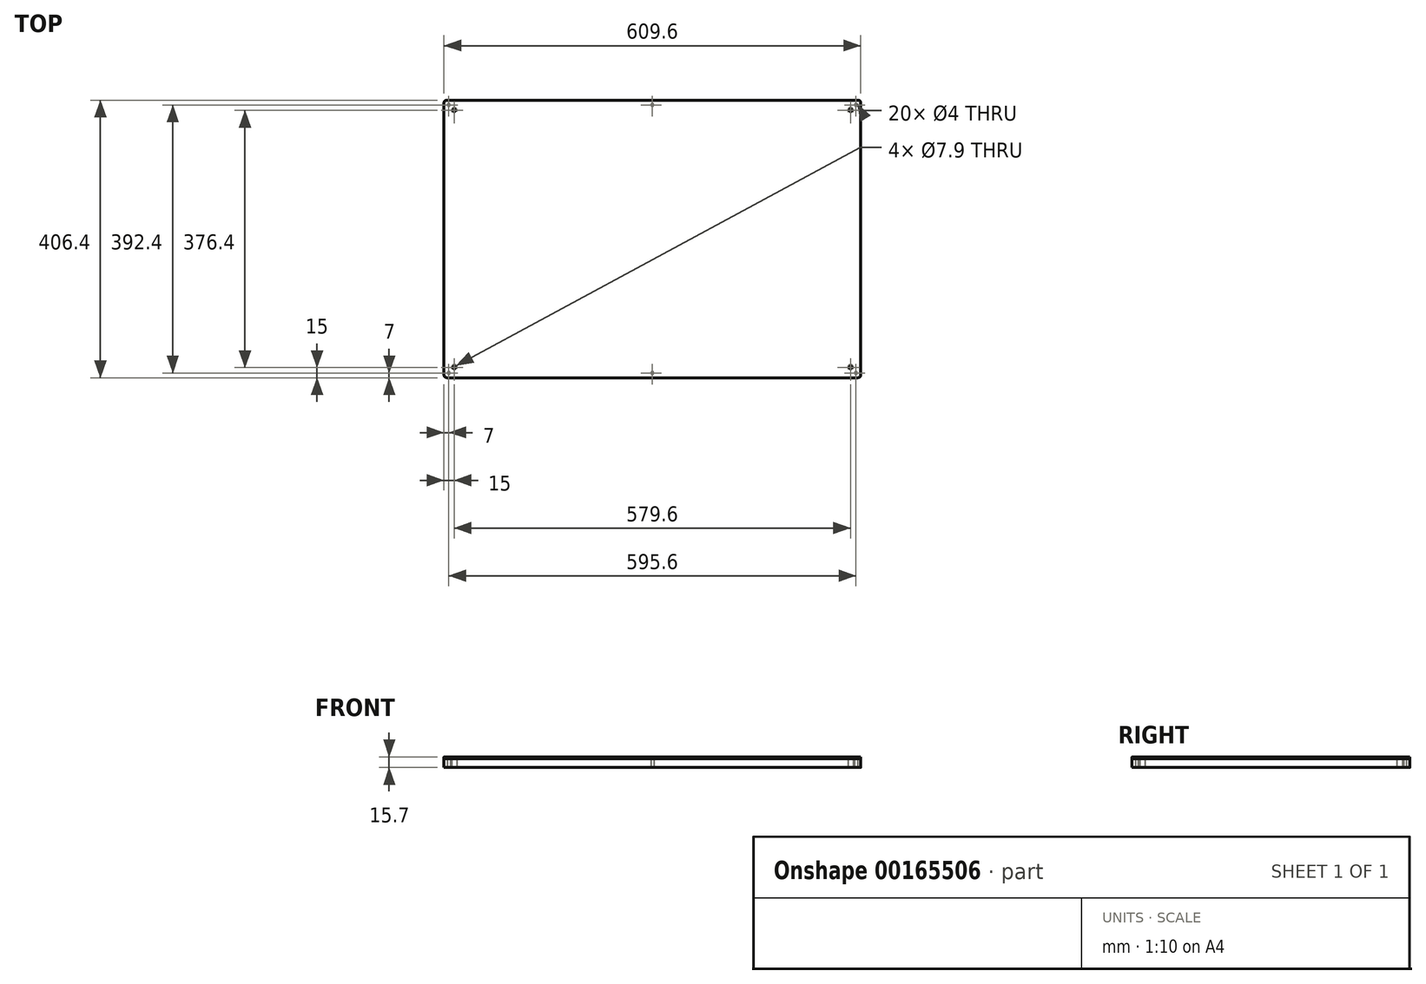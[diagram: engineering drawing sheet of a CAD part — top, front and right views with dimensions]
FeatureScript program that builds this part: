
annotation { "Feature Type Name" : "Feature", "Feature Type Description" : "" }
export const myFeature = defineFeature(function(context is Context, id is Id, definition is map)
    precondition{}
    {
        {
            var Q0;
            Q0=qCreatedBy(makeId("Top.planeOp"),FACE);
            var sketch = newSketch(context, id + "F0", { "sketchPlane" : qUnion([Q0])});
            skLineSegment(sketch, "E0.bottom", {"start": v(304.8, -203.2) * mm, "end": v(-304.8, -203.2) * mm});
            skLineSegment(sketch, "E0.top", {"start": v(304.8, 203.2) * mm, "end": v(-304.8, 203.2) * mm});
            skLineSegment(sketch, "E0.left", {"start": v(304.8, -203.2) * mm, "end": v(304.8, 203.2) * mm});
            skLineSegment(sketch, "E0.right", {"start": v(-304.8, -203.2) * mm, "end": v(-304.8, 203.2) * mm});
            skPoint(sketch, "E0.middle", {"position": v(0, 0) * mm});
            skLineSegment(sketch, "E1.0", {"start": v(297.8, 196.2) * mm, "end": v(-297.8, 196.2) * mm, "construction": true});
            skLineSegment(sketch, "E1.1", {"start": v(297.8, -196.2) * mm, "end": v(297.8, 196.2) * mm, "construction": true});
            skLineSegment(sketch, "E1.2", {"start": v(297.8, -196.2) * mm, "end": v(-297.8, -196.2) * mm, "construction": true});
            skLineSegment(sketch, "E1.3", {"start": v(-297.8, -196.2) * mm, "end": v(-297.8, 196.2) * mm, "construction": true});
            skCircle(sketch, "E2", {"center": v(-297.8, 196.2) * mm, "radius": 2 * mm});
            skCircle(sketch, "E3.MirrorC", {"center": v(297.8, 196.2) * mm, "radius": 2 * mm});
            skCircle(sketch, "E4.MirrorC", {"center": v(-297.8, -196.2) * mm, "radius": 2 * mm});
            skCircle(sketch, "E5.MirrorC", {"center": v(297.8, -196.2) * mm, "radius": 2 * mm});
            skCircle(sketch, "E6", {"center": v(0, 196.2) * mm, "radius": 2 * mm});
            skCircle(sketch, "E7.MirrorC", {"center": v(0, -196.2) * mm, "radius": 2 * mm});
            skLineSegment(sketch, "E8.0", {"start": v(289.8, -188.2) * mm, "end": v(-289.8, -188.2) * mm, "construction": true});
            skLineSegment(sketch, "E8.1", {"start": v(289.8, -188.2) * mm, "end": v(289.8, 188.2) * mm, "construction": true});
            skLineSegment(sketch, "E8.2", {"start": v(289.8, 188.2) * mm, "end": v(-289.8, 188.2) * mm, "construction": true});
            skLineSegment(sketch, "E8.3", {"start": v(-289.8, -188.2) * mm, "end": v(-289.8, 188.2) * mm, "construction": true});
            skCircle(sketch, "E9", {"center": v(-289.8, -188.2) * mm, "radius": 3.95 * mm});
            skCircle(sketch, "E10.MirrorC", {"center": v(-289.8, 188.2) * mm, "radius": 3.95 * mm});
            skCircle(sketch, "E11.MirrorC", {"center": v(289.8, -188.2) * mm, "radius": 3.95 * mm});
            skCircle(sketch, "E12.MirrorC", {"center": v(289.8, 188.2) * mm, "radius": 3.95 * mm});
            skSolve(sketch);
        }
        {
            var Q0;
            Q0 = qSketchRegion(id + "F0", true);
            extrude(context, id + "F1", {"entities" : qUnion([Q0]), "depth" : 12.7 * mm});
        }
        {
            var Q0;
            Q0=makeQuery(id+"F1.opExtrude","CAP_FACE",FACE,{"disambiguationData":[OSD([sQuery(id+"F0.wireOp",EDGE,"E0.bottom"),sQuery(id+"F0.wireOp",EDGE,"E0.top"),sQuery(id+"F0.wireOp",EDGE,"E0.left"),sQuery(id+"F0.wireOp",EDGE,"E0.right"),sQuery(id+"F0.wireOp",EDGE,"E2"),sQuery(id+"F0.wireOp",EDGE,"E3.MirrorC"),sQuery(id+"F0.wireOp",EDGE,"E4.MirrorC"),sQuery(id+"F0.wireOp",EDGE,"E5.MirrorC"),sQuery(id+"F0.wireOp",EDGE,"E6"),sQuery(id+"F0.wireOp",EDGE,"E7.MirrorC")])],"isStart":false});
            var sketch = newSketch(context, id + "F2", { "sketchPlane" : qUnion([Q0])});
            skLineSegment(sketch, "E13.0", {"start": v(304.8, 203.2) * mm, "end": v(-304.8, 203.2) * mm});
            skLineSegment(sketch, "E13.1", {"start": v(-304.8, -203.2) * mm, "end": v(-304.8, 203.2) * mm});
            skLineSegment(sketch, "E13.2", {"start": v(304.8, -203.2) * mm, "end": v(-304.8, -203.2) * mm});
            skLineSegment(sketch, "E13.3", {"start": v(304.8, -203.2) * mm, "end": v(304.8, 203.2) * mm});
            skCircle(sketch, "E13.4", {"center": v(297.8, 196.2) * mm, "radius": 2 * mm});
            skCircle(sketch, "E13.5", {"center": v(0, 196.2) * mm, "radius": 2 * mm});
            skCircle(sketch, "E13.6", {"center": v(-297.8, 196.2) * mm, "radius": 2 * mm});
            skCircle(sketch, "E13.7", {"center": v(-297.8, -196.2) * mm, "radius": 2 * mm});
            skCircle(sketch, "E13.8", {"center": v(0, -196.2) * mm, "radius": 2 * mm});
            skCircle(sketch, "E13.9", {"center": v(297.8, -196.2) * mm, "radius": 2 * mm});
            skCircle(sketch, "E14", {"center": v(-289.8, 188.2) * mm, "radius": 2 * mm});
            skCircle(sketch, "E15.MirrorC", {"center": v(289.8, 188.2) * mm, "radius": 2 * mm});
            skCircle(sketch, "E16.MirrorC", {"center": v(289.8, -188.2) * mm, "radius": 2 * mm});
            skCircle(sketch, "E17.MirrorC", {"center": v(-289.8, -188.2) * mm, "radius": 2 * mm});
            skSolve(sketch);
        }
        {
            var Q0;
            Q0 = qSketchRegion(id + "F2", true);
            extrude(context, id + "F3", {"entities" : qUnion([Q0]), "depth" : 3 * mm});
        }
        {
            var Q0;
            Q0=makeQuery(id+"F1.opExtrude","SWEPT_EDGE",EDGE,{"disambiguationData":[OSD([sQuery(id+"F0.wireOp",EDGE,"E0.bottom"),sQuery(id+"F0.wireOp",EDGE,"E0.right")])]});
            var Q1;
            Q1=makeQuery(id+"F3.opExtrude","SWEPT_EDGE",EDGE,{"disambiguationData":[OSD([sQuery(id+"F2.wireOp",EDGE,"E13.1"),sQuery(id+"F2.wireOp",EDGE,"E13.2")])]});
            var Q2;
            Q2=makeQuery(id+"F1.opExtrude","SWEPT_EDGE",EDGE,{"disambiguationData":[OSD([sQuery(id+"F0.wireOp",EDGE,"E0.top"),sQuery(id+"F0.wireOp",EDGE,"E0.right")])]});
            var Q3;
            Q3=makeQuery(id+"F3.opExtrude","SWEPT_EDGE",EDGE,{"disambiguationData":[OSD([sQuery(id+"F2.wireOp",EDGE,"E13.0"),sQuery(id+"F2.wireOp",EDGE,"E13.1")])]});
            var Q4;
            Q4=makeQuery(id+"F1.opExtrude","SWEPT_EDGE",EDGE,{"disambiguationData":[OSD([sQuery(id+"F0.wireOp",EDGE,"E0.bottom"),sQuery(id+"F0.wireOp",EDGE,"E0.left")])]});
            var Q5;
            Q5=makeQuery(id+"F3.opExtrude","SWEPT_EDGE",EDGE,{"disambiguationData":[OSD([sQuery(id+"F2.wireOp",EDGE,"E13.2"),sQuery(id+"F2.wireOp",EDGE,"E13.3")])]});
            var Q6;
            Q6=makeQuery(id+"F1.opExtrude","SWEPT_EDGE",EDGE,{"disambiguationData":[OSD([sQuery(id+"F0.wireOp",EDGE,"E0.top"),sQuery(id+"F0.wireOp",EDGE,"E0.left")])]});
            var Q7;
            Q7=makeQuery(id+"F3.opExtrude","SWEPT_EDGE",EDGE,{"disambiguationData":[OSD([sQuery(id+"F2.wireOp",EDGE,"E13.0"),sQuery(id+"F2.wireOp",EDGE,"E13.3")])]});
            fillet(context, id + "F4", {"entities" : qUnion([Q0, Q1, Q2, Q3, Q4, Q5, Q6, Q7]), "radius" : 4 * mm, "tangentPropagation" : true, "allowEdgeOverflow" : false});
        }
        {
            var Q0;
            Q0=makeQuery(id+"F3.opExtrude","CAP_FACE",FACE,{"disambiguationData":[OSD([sQuery(id+"F2.wireOp",EDGE,"E13.0"),sQuery(id+"F2.wireOp",EDGE,"E13.1"),sQuery(id+"F2.wireOp",EDGE,"E13.2"),sQuery(id+"F2.wireOp",EDGE,"E13.3"),sQuery(id+"F2.wireOp",EDGE,"E13.4"),sQuery(id+"F2.wireOp",EDGE,"E13.5"),sQuery(id+"F2.wireOp",EDGE,"E13.6"),sQuery(id+"F2.wireOp",EDGE,"E13.7"),sQuery(id+"F2.wireOp",EDGE,"E13.8"),sQuery(id+"F2.wireOp",EDGE,"E13.9"),sQuery(id+"F2.wireOp",EDGE,"E14"),sQuery(id+"F2.wireOp",EDGE,"E15.MirrorC"),sQuery(id+"F2.wireOp",EDGE,"E16.MirrorC"),sQuery(id+"F2.wireOp",EDGE,"E17.MirrorC")])],"isStart":false});
            var sketch = newSketch(context, id + "F5", { "sketchPlane" : qUnion([Q0])});
            skLineSegment(sketch, "E18.0", {"start": v(300.8, -203.2) * mm, "end": v(-300.8, -203.2) * mm});
            skArc(sketch, "E18.1", {"start": v(-304.8, -199.2) * mm, "mid": v(-303.63, -202.03) * mm, "end": v(-300.8, -203.2) * mm});
            skLineSegment(sketch, "E18.2", {"start": v(-304.8, -199.2) * mm, "end": v(-304.8, 199.2) * mm});
            skArc(sketch, "E18.3", {"start": v(-300.8, 203.2) * mm, "mid": v(-303.63, 202.03) * mm, "end": v(-304.8, 199.2) * mm});
            skLineSegment(sketch, "E18.4", {"start": v(300.8, 203.2) * mm, "end": v(-300.8, 203.2) * mm});
            skArc(sketch, "E18.5", {"start": v(304.8, 199.2) * mm, "mid": v(303.63, 202.03) * mm, "end": v(300.8, 203.2) * mm});
            skLineSegment(sketch, "E18.6", {"start": v(304.8, -199.2) * mm, "end": v(304.8, 199.2) * mm});
            skArc(sketch, "E18.7", {"start": v(300.8, -203.2) * mm, "mid": v(303.63, -202.03) * mm, "end": v(304.8, -199.2) * mm});
            skCircle(sketch, "E18.8", {"center": v(289.8, -188.2) * mm, "radius": 2 * mm});
            skCircle(sketch, "E18.9", {"center": v(-289.8, -188.2) * mm, "radius": 2 * mm});
            skCircle(sketch, "E18.10", {"center": v(-289.8, 188.2) * mm, "radius": 2 * mm});
            skCircle(sketch, "E18.11", {"center": v(289.8, 188.2) * mm, "radius": 2 * mm});
            skSolve(sketch);
        }
        {
            var Q0;
            Q0 = qSketchRegion(id + "F5", true);
            extrude(context, id + "F6", {"entities" : qUnion([Q0]), "depth" : 1 / 203.2 * mm});
        }
    });
